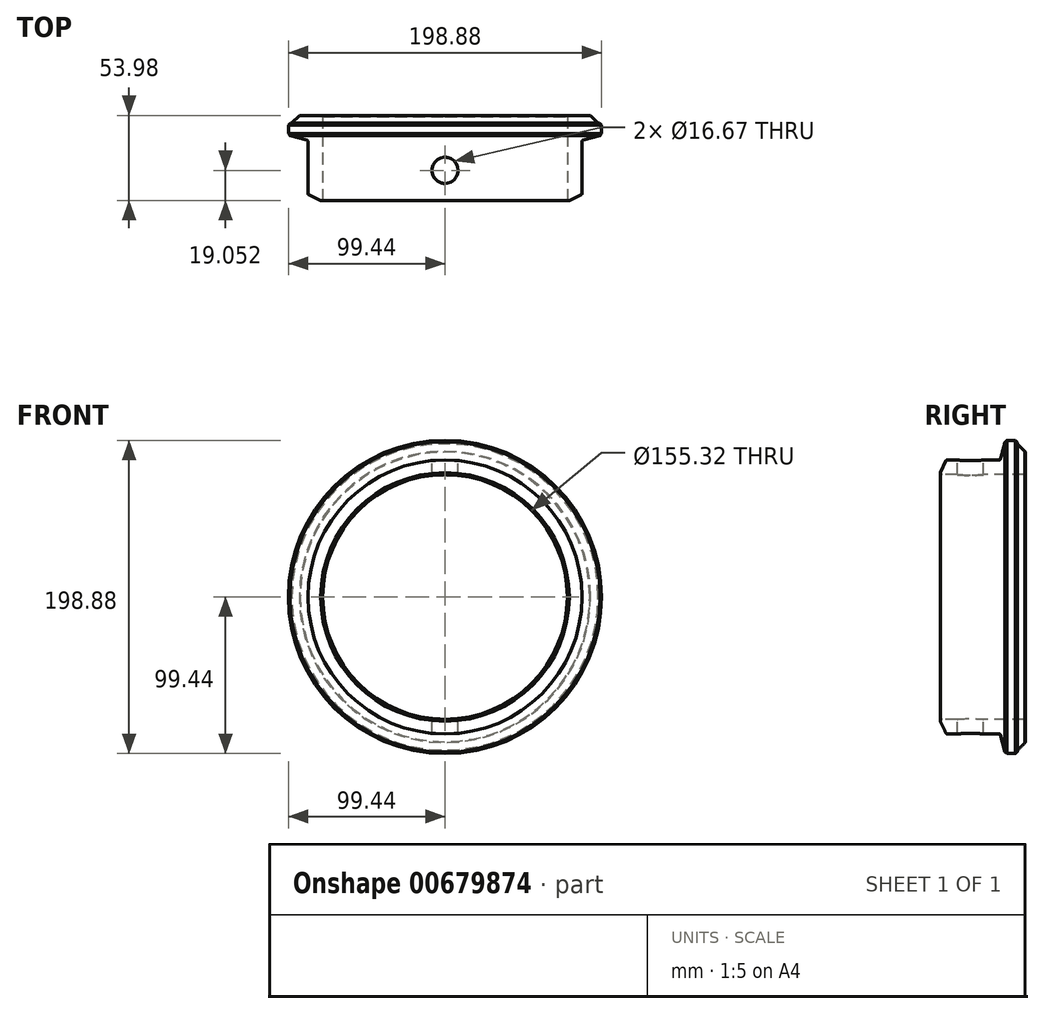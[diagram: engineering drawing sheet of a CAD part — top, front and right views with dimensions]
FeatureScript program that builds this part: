
annotation { "Feature Type Name" : "Feature", "Feature Type Description" : "" }
export const myFeature = defineFeature(function(context is Context, id is Id, definition is map)
    precondition{}
    {
        {
            var Q0;
            Q0=qCreatedBy(makeId("Right.planeOp"),FACE);
            var sketch = newSketch(context, id + "F0", { "sketchPlane" : qUnion([Q0])});
            skLineSegment(sketch, "E0", {"start": v(-26.23, 77.66) * mm, "end": v(26.23, 77.66) * mm});
            skPoint(sketch, "E1", {"position": v(0, 77.66) * mm});
            skLineSegment(sketch, "E2", {"start": v(26.99, 77.66) * mm, "end": v(26.99, 92.27) * mm});
            skLineSegment(sketch, "E3", {"start": v(21.96, 97.3) * mm, "end": v(21.96, 99.44) * mm});
            skLineSegment(sketch, "E4", {"start": v(21.96, 99.44) * mm, "end": v(14.32, 99.44) * mm});
            skLineSegment(sketch, "E5", {"start": v(14.32, 99.44) * mm, "end": v(10.99, 87) * mm});
            skLineSegment(sketch, "E6", {"start": v(10.99, 87) * mm, "end": v(-23.23, 87) * mm});
            skLineSegment(sketch, "E7", {"start": v(-23.23, 87) * mm, "end": v(-26.99, 78.93) * mm});
            skLineSegment(sketch, "E8", {"start": v(-26.99, 78.42) * mm, "end": v(-26.99, 78.39) * mm});
            skPoint(sketch, "E9.visualSharp", {"position": v(26.99, 77.66) * mm});
            skPoint(sketch, "E10.visualSharp", {"position": v(-26.99, 77.66) * mm});
            skPoint(sketch, "E11.visualSharp", {"position": v(10.99, 87) * mm});
            skPoint(sketch, "E12.visualSharp", {"position": v(-26.99, 78.93) * mm});
            skPoint(sketch, "E13.visualSharp", {"position": v(21.96, 97.3) * mm});
            skPoint(sketch, "E14.visualSharp", {"position": v(26.99, 92.27) * mm});
            skLineSegment(sketch, "E15", {"start": v(-57.68, 0) * mm, "end": v(44.18, 0) * mm, "construction": true});
            skLineSegment(sketch, "E16", {"start": v(26.99, 77.66) * mm, "end": v(-26.99, 77.66) * mm});
            skLineSegment(sketch, "E17", {"start": v(-26.99, 78.93) * mm, "end": v(-26.99, 77.66) * mm});
            skLineSegment(sketch, "E18", {"start": v(21.96, 97.3) * mm, "end": v(26.99, 92.27) * mm});
            skSolve(sketch);
        }
        {
            var Q0;
            {var subQ1=sQuery(id+"F0.wireOp",EDGE,"E2");Q0=makeQuery(id+"F0.imprint","IMPRINT",FACE,{"disambiguationData":[TD([[makeQuery(id+"F0.imprint","IMPRINT",EDGE,{"derivedFrom":subQ1}),1.0]])]});}
            var Q1;
            Q1=sQuery(id+"F0.wireOp",EDGE,"E15");
            revolve(context, id + "F1", {"entities" : qUnion([Q0]), "axis" : qUnion([Q1]), "revolveType" : RevolveType.FULL});
        }
        {
            var Q0;
            Q0=makeQuery(id+"F1.opRevolve","SWEPT_EDGE",EDGE,{"disambiguationData":[OSD([sQuery(id+"F0.wireOp",EDGE,"E4"),sQuery(id+"F0.wireOp",EDGE,"E5")])]});
            var Q1;
            Q1=makeQuery(id+"F1.opRevolve","SWEPT_EDGE",EDGE,{"disambiguationData":[OSD([sQuery(id+"F0.wireOp",EDGE,"E3"),sQuery(id+"F0.wireOp",EDGE,"E4")])]});
            chamfer(context, id + "F2", {"entities" : qUnion([Q0, Q1]), "width" : 1.27 * mm, "tangentPropagation" : true});
        }
        {
            var Q0;
            Q0=qCreatedBy(makeId("Top.planeOp"),FACE);
            cPlane(context, id + "F3", {"entities" : qUnion([Q0]), "cplaneType" : CPlaneType.OFFSET, "offset" : 87 * mm, "width" : 152.4 * mm, "height" : 152.4 * mm});
        }
        {
            var Q0;
            Q0=qCreatedBy(id+"F3.planeOp",FACE);
            var sketch = newSketch(context, id + "F4", { "sketchPlane" : qUnion([Q0])});
            skCircle(sketch, "E19", {"center": v(0, -7.94) * mm, "radius": 8.33 * mm});
            skSolve(sketch);
        }
        {
            var Q0;
            Q0=makeQuery(id+"F4.imprint","IMPRINT",FACE,{"disambiguationData":[TD([[makeQuery(id+"F4.imprint","IMPRINT",EDGE,{"derivedFrom":sQuery(id+"F4.wireOp",EDGE,"E19")}),1.0]])]});
            extrude(context, id + "F5", {"entities" : qUnion([Q0]), "operationType" : NewBodyOperationType.REMOVE, "oppositeDirection" : true, "depth" : 203.2 * mm, "offsetDistance" : 25.4 * mm});
        }
        {
            var Q0;
            Q0=makeQuery(id+"F1.opRevolve","SWEPT_EDGE",EDGE,{"disambiguationData":[OSD([sQuery(id+"F0.wireOp",EDGE,"E2"),sQuery(id+"F0.wireOp",EDGE,"UZKI4Nwt-nGWC-WsZ3-0cs7-JIA6lq6C3uto")])]});
            chamfer(context, id + "F6", {"entities" : qUnion([Q0]), "width" : 0.76 * mm, "tangentPropagation" : true});
        }
        {
            var Q0;
            Q0=makeQuery(id+"F1.opRevolve","SWEPT_EDGE",EDGE,{"disambiguationData":[OSD([sQuery(id+"F0.wireOp",EDGE,"E6"),sQuery(id+"F0.wireOp",EDGE,"E7")])]});
            var Q1;
            Q1=makeQuery(id+"F1.opRevolve","SWEPT_EDGE",EDGE,{"disambiguationData":[OSD([sQuery(id+"F0.wireOp",EDGE,"E5"),sQuery(id+"F0.wireOp",EDGE,"E6")])]});
            fillet(context, id + "F7", {"entities" : qUnion([Q0, Q1]), "radius" : 0.76 * mm, "tangentPropagation" : true, "allowEdgeOverflow" : false});
        }
        {
            var Q0;
            Q0=makeQuery(id+"F1.opRevolve","SWEPT_EDGE",EDGE,{"disambiguationData":[OSD([sQuery(id+"F0.wireOp",EDGE,"E2"),sQuery(id+"F0.wireOp",EDGE,"E16")])]});
            var Q1;
            Q1=makeQuery(id+"F1.opRevolve","SWEPT_EDGE",EDGE,{"disambiguationData":[OSD([sQuery(id+"F0.wireOp",EDGE,"E16"),sQuery(id+"F0.wireOp",EDGE,"E17")])]});
            fillet(context, id + "F8", {"entities" : qUnion([Q0, Q1]), "radius" : 1.27 * mm, "tangentPropagation" : true, "allowEdgeOverflow" : false});
        }
    });
